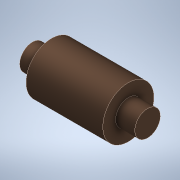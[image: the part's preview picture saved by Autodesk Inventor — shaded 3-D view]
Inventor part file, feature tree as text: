
AUTODESK INVENTOR PART (.ipt)
format: ipt  version: 2021 (Build 250183000, 183)  size: 122,368 bytes
history: native  units: mm
features: extrude x4, sketch x4
ambient origin geometry x8: Origin, YZ Plane, XZ Plane, XY Plane, X Axis, Y Axis, Z Axis, Center Point
bodies: Body1 (feature_tree)
feature tree (8):
  extrude  "Extrusion2"  Depth=15.0mm TaperAngle=0.0deg
  extrude  "Extrusion3"  Depth=90.0mm TaperAngle=0.0deg
  extrude  "Extrusion4"  Depth=20.0mm
  extrude  "Extrusion5"  Depth=15.0mm TaperAngle=0.0deg
  sketch  "Sketch2"  dims[d5=20.0mm d6=15.0mm d7=0.0mm]
  sketch  "Sketch3"  dims[d8=40.0mm d9=90.0mm d10=0.0mm]
  sketch  "Sketch4"  dims[d11=20.0mm d12=40.0mm]
  sketch  "Sketch5"  dims[d13=30.0mm d14=0.0mm d15=15.0mm d16=0.0mm]
